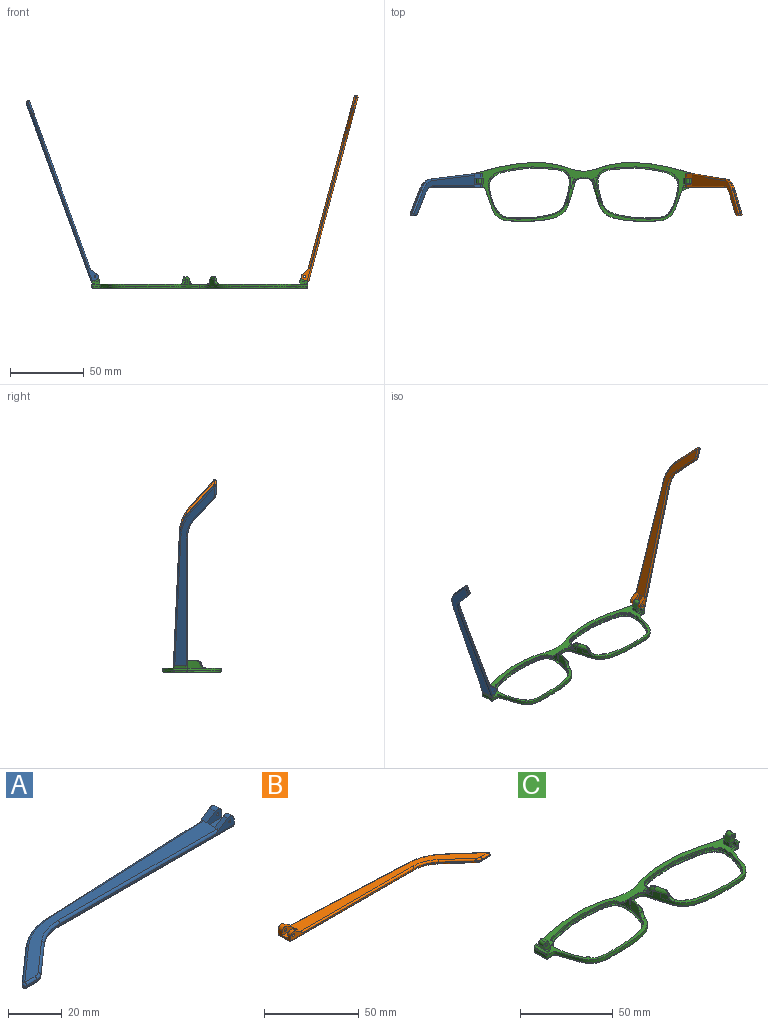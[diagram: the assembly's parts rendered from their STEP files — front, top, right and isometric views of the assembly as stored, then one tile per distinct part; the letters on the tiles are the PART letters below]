
ASSEMBLY  parts=3 mates=2
PART A: 43 faces, bbox 130.2x29.5x5.9 mm
  f0: plane 9.62x3.72mm, normal (1,0,0), area 24.7mm2, adj f1,f3,f4,f5,f10,f16,f18,f28
  f1: cylinder r=2.2mm len=3.45mm, axis (0,-1,0), area 11mm2, adj f0,f2,f4,f37
  f2: plane 6.01x3.91mm, normal (-0.55,0,0.84), area 12.7mm2, adj f1,f4,f9,f19,f37
  f3: plane 2.26x0.1mm, normal (0,0,1), area 0.1mm2, adj f0,f5,f18
  f4: plane 92.1x4.9mm, normal (0,-1,0), area 79.9mm2, adj f0,f1,f2,f14,f19,f36,f42
  f5: plane 93.42x4.13mm, normal (-0.04,1,0), area 64.8mm2, adj f0,f3,f11,f15,f17,f27,f28
  f6: plane 17.82x15.72mm, normal (-0.66,0.75,0), area 14.3mm2, adj f11,f12,f25,f30
  f7: plane 5.46x0.6mm, normal (0,-1,0), area 3.3mm2, adj f12,f13,f23,f32
  f8: plane 14.99x13.23mm, normal (0.66,-0.75,0), area 12mm2, adj f13,f14,f21,f34
  f9: plane 121.18x26.73mm, normal (0,0,1), area 627.7mm2, adj f2,f17,f19,f20,f21,f22,f23,f25
  f10: plane 129.1x27.08mm, normal (0,0,-1), area 686.5mm2, adj f0,f28,f29,f30,f32,f33,f34,f35
  f11: cylinder r=30mm len=18.52mm, axis (0,0,-1), area 12.2mm2, adj f5,f6,f26,f29
  f12: cylinder r=1mm len=1.75mm, axis (0,0,-1), area 1.5mm2, adj f6,f7,f24,f31
  f13: cylinder r=5mm len=3.31mm, axis (0,0,-1), area 2.2mm2, adj f7,f8,f22,f33
  f14: cylinder r=20mm len=13.23mm, axis (0,0,1), area 8.7mm2, adj f4,f8,f20,f35
  f15: plane 5.66x0.25mm, normal (0,0,-1), area 0.7mm2, adj f5,f17,f18
  f16: cylinder r=2.2mm len=3.45mm, axis (0,-1,0), area 14.8mm2, adj f0,f17,f18,f38
  f17: plane 6.01x3.91mm, normal (-0.55,0,0.84), area 16.9mm2, adj f5,f9,f15,f16,f18,f27,f38
  f18: plane 7.92x3.3mm, normal (0,1,0), area 15.9mm2, adj f0,f3,f15,f16,f17,f41
  f19: cylinder r=1mm len=84.18mm, axis (-1,0,0), area 131.4mm2, adj f2,f4,f9,f20
  f20: torus R=21mm, axis (0,0,1), area 23.1mm2, adj f9,f14,f19,f21
  f21: cylinder r=1mm len=15.65mm, axis (-0.75,-0.66,0), area 31.4mm2, adj f8,f9,f20,f22
  f22: torus R=4mm, axis (0,0,1), area 5.3mm2, adj f9,f13,f21,f23
  f23: cylinder r=1mm len=5.46mm, axis (-1,0,0), area 8.6mm2, adj f7,f9,f22,f24
  f24: sphere r=1mm, area 2.4mm2, adj f12,f23,f25
  f25: cylinder r=1mm len=18.48mm, axis (0.75,0.66,0), area 37.3mm2, adj f6,f9,f24,f26
  f26: torus R=29mm, axis (0,0,1), area 31.6mm2, adj f9,f11,f25,f27
  f27: cylinder r=1mm len=85.5mm, axis (1,0.04,0), area 133.5mm2, adj f5,f9,f17,f26
  f28: cylinder r=1mm len=93.46mm, axis (-1,-0.04,0), area 146.9mm2, adj f0,f5,f10,f29
  f29: torus R=29mm, axis (0,0,1), area 31.6mm2, adj f10,f11,f28,f30
  f30: cylinder r=1mm len=18.48mm, axis (-0.75,-0.66,0), area 37.3mm2, adj f6,f10,f29,f31
  f31: sphere r=1mm, area 2.4mm2, adj f12,f30,f32
  f32: cylinder r=1mm len=5.46mm, axis (1,0,0), area 8.6mm2, adj f7,f10,f31,f33
  f33: torus R=4mm, axis (0,0,1), area 5.3mm2, adj f10,f13,f32,f34
  f34: cylinder r=1mm len=15.65mm, axis (0.75,0.66,0), area 31.4mm2, adj f8,f10,f33,f35
  f35: torus R=21mm, axis (0,0,1), area 23.1mm2, adj f10,f14,f34,f36
  f36: cylinder r=1mm len=92.1mm, axis (1,0,0), area 144.7mm2, adj f0,f4,f10,f35
  f37: plane 7.92x4.7mm, normal (0,1,0), area 27mm2, adj f0,f1,f2,f39,f40,f42
  f38: plane 7.92x4.7mm, normal (0,-1,0), area 27mm2, adj f0,f16,f17,f39,f40,f41
  f39: plane 7.92x4.1mm, normal (0,0,1), area 32.5mm2, adj f0,f37,f38,f40
  f40: plane 4.1x1.4mm, normal (1,0,0), area 5.7mm2, adj f9,f37,f38,f39
  f41: cylinder r=0.5mm len=3.1mm, axis (0,-1,0), area 9.7mm2, adj f18,f38
  f42: cylinder r=0.5mm len=2.3mm, axis (0,-1,0), area 7.2mm2, adj f4,f37
PART B: 43 faces, bbox 130.2x29.5x5.9 mm
  f0: plane 9.62x3.72mm, normal (-1,0,0), area 24.7mm2, adj f1,f3,f4,f5,f10,f16,f18,f28
  f1: cylinder r=2.2mm len=3.45mm, axis (0,-1,0), area 11mm2, adj f0,f2,f4,f37
  f2: plane 6.01x3.91mm, normal (0.55,0,0.84), area 12.7mm2, adj f1,f4,f9,f19,f37
  f3: plane 2.26x0.1mm, normal (0,0,1), area 0.1mm2, adj f0,f5,f18
  f4: plane 92.1x4.9mm, normal (0,-1,0), area 78.2mm2, adj f0,f1,f2,f14,f19,f36,f42
  f5: plane 93.42x4.13mm, normal (0.04,1,0), area 64.8mm2, adj f0,f3,f11,f15,f17,f27,f28
  f6: plane 17.82x15.72mm, normal (0.66,0.75,0), area 14.3mm2, adj f11,f12,f25,f30
  f7: plane 5.46x0.6mm, normal (0,-1,0), area 3.3mm2, adj f12,f13,f23,f32
  f8: plane 14.99x13.23mm, normal (-0.66,-0.75,0), area 12mm2, adj f13,f14,f21,f34
  f9: plane 121.18x26.73mm, normal (0,0,1), area 627.7mm2, adj f2,f17,f19,f20,f21,f22,f23,f25
  f10: plane 129.1x27.08mm, normal (0,0,-1), area 686.5mm2, adj f0,f28,f29,f30,f32,f33,f34,f35
  f11: cylinder r=30mm len=18.52mm, axis (0,0,-1), area 12.2mm2, adj f5,f6,f26,f29
  f12: cylinder r=1mm len=1.75mm, axis (0,0,-1), area 1.5mm2, adj f6,f7,f24,f31
  f13: cylinder r=5mm len=3.31mm, axis (0,0,-1), area 2.2mm2, adj f7,f8,f22,f33
  f14: cylinder r=20mm len=13.23mm, axis (0,0,1), area 8.7mm2, adj f4,f8,f20,f35
  f15: plane 5.66x0.25mm, normal (0,0,-1), area 0.7mm2, adj f5,f17,f18
  f16: cylinder r=2.2mm len=3.45mm, axis (0,-1,0), area 14.8mm2, adj f0,f17,f18,f38
  f17: plane 6.01x3.91mm, normal (0.55,0,0.84), area 16.9mm2, adj f5,f9,f15,f16,f18,f27,f38
  f18: plane 7.92x3.3mm, normal (0,1,0), area 14.3mm2, adj f0,f3,f15,f16,f17,f41
  f19: cylinder r=1mm len=84.18mm, axis (1,0,0), area 131.4mm2, adj f2,f4,f9,f20
  f20: torus R=21mm, axis (0,0,1), area 23.1mm2, adj f9,f14,f19,f21
  f21: cylinder r=1mm len=15.65mm, axis (0.75,-0.66,0), area 31.4mm2, adj f8,f9,f20,f22
  f22: torus R=4mm, axis (0,0,1), area 5.3mm2, adj f9,f13,f21,f23
  f23: cylinder r=1mm len=5.46mm, axis (1,0,0), area 8.6mm2, adj f7,f9,f22,f24
  f24: sphere r=1mm, area 2.4mm2, adj f12,f23,f25
  f25: cylinder r=1mm len=18.48mm, axis (-0.75,0.66,0), area 37.3mm2, adj f6,f9,f24,f26
  f26: torus R=29mm, axis (0,0,1), area 31.6mm2, adj f9,f11,f25,f27
  f27: cylinder r=1mm len=85.5mm, axis (-1,0.04,0), area 133.5mm2, adj f5,f9,f17,f26
  f28: cylinder r=1mm len=93.46mm, axis (1,-0.04,0), area 146.9mm2, adj f0,f5,f10,f29
  f29: torus R=29mm, axis (0,0,1), area 31.6mm2, adj f10,f11,f28,f30
  f30: cylinder r=1mm len=18.48mm, axis (0.75,-0.66,0), area 37.3mm2, adj f6,f10,f29,f31
  f31: sphere r=1mm, area 2.4mm2, adj f12,f30,f32
  f32: cylinder r=1mm len=5.46mm, axis (-1,0,0), area 8.6mm2, adj f7,f10,f31,f33
  f33: torus R=4mm, axis (0,0,1), area 5.3mm2, adj f10,f13,f32,f34
  f34: cylinder r=1mm len=15.65mm, axis (-0.75,0.66,0), area 31.4mm2, adj f8,f10,f33,f35
  f35: torus R=21mm, axis (0,0,1), area 23.1mm2, adj f10,f14,f34,f36
  f36: cylinder r=1mm len=92.1mm, axis (-1,0,0), area 144.7mm2, adj f0,f4,f10,f35
  f37: plane 7.92x4.7mm, normal (0,1,0), area 25.4mm2, adj f0,f1,f2,f39,f40,f42
  f38: plane 7.92x4.7mm, normal (0,-1,0), area 25.4mm2, adj f0,f16,f17,f39,f40,f41
  f39: plane 7.92x4.1mm, normal (0,0,1), area 32.5mm2, adj f0,f37,f38,f40
  f40: plane 4.1x1.4mm, normal (-1,0,0), area 5.7mm2, adj f9,f37,f38,f39
  f41: cylinder r=0.88mm len=3.1mm, axis (0,-1,0), area 17mm2, adj f18,f38
  f42: cylinder r=0.88mm len=2.3mm, axis (0,-1,0), area 12.6mm2, adj f4,f37
PART C: 118 faces, bbox 148.1x40.9x17.9 mm
  f0: bspline ~1.82x1.22mm, area 0.7mm2, adj f2,f7,f37,f52
  f1: plane 147.69x40.46mm, normal (0,0,1), area 858.2mm2, adj f4,f5,f6,f7,f8,f12,f20,f23
  f2: bspline ~6.1x4.93mm, area 12.7mm2, adj f0,f7,f37,f41,f43,f52,f53
  f3: plane 4.46x1.45mm, normal (0,0,1), area 0.1mm2, adj f7,f38
  f4: plane 1.23x0.04mm, normal (0,0,1), area 0mm2, adj f1,f7,f22
  f5: plane 6.97x5.07mm, normal (0,1,0), area 22.7mm2, adj f1,f20,f21,f25,f27,f28,f30,f31
  f6: plane 3.2x2.36mm, normal (0,-1,0), area 5.7mm2, adj f1,f20,f26,f29
  f7: extruded ~73.26x39.84mm, area 292.7mm2, adj f0,f1,f2,f3,f4,f8,f13,f14
  f8: extruded ~35.39x5.69mm, area 72.2mm2, adj f1,f7,f18,f67
  f9: plane 144.78x37.85mm, normal (0,0,-1), area 582.4mm2, adj f13,f15,f17,f18,f19,f71,f73,f75
  f10: plane 56.06x35.45mm, normal (0,0,1), area 127mm2, adj f11,f19
  f11: extruded ~55.69x35.36mm, area 160.5mm2, adj f10,f12
  f12: extruded ~55.69x35.36mm, area 226.3mm2, adj f1,f11,f39,f40,f41,f42,f43,f44
  f13: bspline ~73.27x30.39mm, area 161.7mm2, adj f7,f9,f14,f71
  f14: bspline ~1x1mm, area 0.8mm2, adj f7,f13,f15
  f15: bspline ~8.99x1.23mm, area 12.6mm2, adj f7,f9,f14,f16
  f16: bspline ~1.04x1mm, area 0.7mm2, adj f7,f15,f17
  f17: bspline ~45.86x8.59mm, area 59.8mm2, adj f7,f9,f16,f18
  f18: bspline ~37.01x6.7mm, area 56.6mm2, adj f8,f9,f17,f76
  f19: bspline ~56.23x35.9mm, area 235.3mm2, adj f9,f10
  f20: plane 4x2.36mm, normal (-1,0,0), area 9.5mm2, adj f1,f5,f6,f21
  f21: plane 4x0.02mm, normal (0.34,0,0.94), area 0.1mm2, adj f5,f20,f28
  f22: plane 2.76x2.53mm, normal (0,-1,0), area 3.9mm2, adj f4,f26,f27,f35,f56
  f23: plane 7.67x1.6mm, normal (0.94,0,-0.34), area 13mm2, adj f1,f35,f36,f56
  f24: plane 2.1x1.69mm, normal (0,1,0), area 2.8mm2, adj f1,f25,f27,f36,f56
  f25: plane 3.3x2.1mm, normal (-1,0,0), area 6.9mm2, adj f1,f5,f24,f27
  f26: plane 2.35x2.1mm, normal (-1,0,0), area 4.9mm2, adj f1,f6,f22,f27,f29
  f27: plane 9.65x1.24mm, normal (0,0,1), area 8.2mm2, adj f5,f22,f24,f25,f26,f29,f30,f56
  f28: plane 4x3.31mm, normal (-0.94,0,0.34), area 14.1mm2, adj f5,f21,f29,f32
  f29: plane 5.77x5.06mm, normal (0,-1,0), area 17mm2, adj f6,f26,f27,f28,f30,f31,f32,f33
  f30: plane 4x2.21mm, normal (0.94,0,-0.34), area 9.4mm2, adj f5,f27,f29,f33
  f31: plane 4x0.01mm, normal (0.34,0,0.94), area 0mm2, adj f5,f29,f32,f33
  f32: cylinder r=1.98mm len=4mm, axis (0,1,0), area 12.4mm2, adj f5,f28,f29,f31
  f33: cylinder r=1.98mm len=4mm, axis (0,-1,0), area 12.4mm2, adj f5,f29,f30,f31
  f34: cylinder r=0.88mm len=4mm, axis (0,-1,0), area 22mm2, adj f5,f29
  f35: cone r=1mm half-angle=20deg, axis (0,0,1), area 2.3mm2, adj f1,f22,f23,f56
  f36: cylinder r=1mm len=2.28mm, axis (-0.34,0,-0.94), area 3mm2, adj f1,f23,f24,f56
  f37: extruded ~3.67x3.11mm, area 5.9mm2, adj f0,f2,f7,f59
  f38: extruded ~4.44x3.32mm, area 15.1mm2, adj f3,f7,f42,f43,f55
  f39: extruded ~4.98x1.37mm, area 6.6mm2, adj f12,f41
  f40: plane 3.63x0.97mm, normal (0,0,1), area 0.3mm2, adj f12,f41,f43
  f41: bspline ~15.5x15.35mm, area 6.4mm2, adj f2,f12,f39,f40,f54
  f42: bspline ~7.26x7.26mm, area 6.3mm2, adj f12,f38,f43,f55
  f43: bspline ~10.29x4.84mm, area 21.4mm2, adj f2,f7,f12,f38,f40,f42
  f44: plane 3.19x1.37mm, normal (0,0,-1), area 2.1mm2, adj f12,f45
  f45: cylinder r=2.28mm len=3.17mm, axis (0,0,1), area 2.1mm2, adj f1,f12,f44,f54
  f46: plane 3.14x2.79mm, normal (0,0,-1), area 3.9mm2, adj f12,f47
  f47: cylinder r=2.28mm len=3.13mm, axis (0,0,1), area 2.5mm2, adj f1,f12,f46
  f48: plane 1.79x1.31mm, normal (0,0,-1), area 0.9mm2, adj f12,f49
  f49: cylinder r=1.3mm len=1.78mm, axis (0,0,1), area 1.3mm2, adj f1,f12,f48
  f50: plane 1.95x1.68mm, normal (0,0,-1), area 1.5mm2, adj f12,f51
  f51: cylinder r=1.3mm len=1.93mm, axis (0,0,1), area 1.5mm2, adj f1,f12,f50
  f52: bspline ~2.66x2.04mm, area 1.9mm2, adj f0,f2,f7,f53,f58
  f53: bspline ~3.55x3.47mm, area 3.7mm2, adj f1,f2,f52,f54,f58
  f54: bspline ~5.1x3.97mm, area 7.9mm2, adj f1,f12,f41,f45,f53
  f55: bspline ~3.7x3.66mm, area 7.8mm2, adj f1,f7,f12,f38,f42
  f56: plane 9.71x1.44mm, normal (0.34,0,0.94), area 13.9mm2, adj f22,f23,f24,f27,f35,f36
  f57: bspline ~6.38x2.14mm, area 2.6mm2, adj f1,f7,f58,f115
  f58: bspline ~2.1x1.46mm, area 0.6mm2, adj f7,f52,f53,f57
  f59: bspline ~5.24x1.75mm, area 0mm2, adj f7,f37
  f60: bspline ~2.19x1.4mm, area 0.7mm2, adj f61,f66,f95,f110
  f61: bspline ~6.1x4.93mm, area 12.6mm2, adj f60,f66,f95,f99,f101,f110,f111
  f62: plane 4.46x1.45mm, normal (0,0,1), area 0.1mm2, adj f66,f96
  f63: plane 1.23x0.04mm, normal (0,0,1), area 0mm2, adj f1,f66,f80
  f64: plane 6.97x5.07mm, normal (0,1,0), area 22.7mm2, adj f1,f78,f79,f83,f85,f86,f88,f89
  f65: plane 3.2x2.36mm, normal (0,-1,0), area 5.7mm2, adj f1,f78,f84,f87
  f66: extruded ~73.26x39.84mm, area 292.7mm2, adj f1,f7,f60,f61,f62,f63,f67,f71
  f67: extruded ~35.39x5.69mm, area 72.2mm2, adj f1,f8,f66,f76
  f68: plane 56.06x35.45mm, normal (0,0,1), area 127mm2, adj f69,f77
  f69: extruded ~55.69x35.36mm, area 160.5mm2, adj f68,f70
  f70: extruded ~55.69x35.36mm, area 226.4mm2, adj f1,f69,f97,f98,f99,f100,f101,f102
  f71: bspline ~73.83x30.39mm, area 161.7mm2, adj f9,f13,f66,f72
  f72: bspline ~1x1mm, area 0.8mm2, adj f66,f71,f73
  f73: bspline ~8.99x1.23mm, area 12.6mm2, adj f9,f66,f72,f74
  f74: bspline ~1.04x1mm, area 0.8mm2, adj f66,f73,f75
  f75: bspline ~45.86x8.59mm, area 59.8mm2, adj f9,f66,f74,f76
  f76: bspline ~37.01x6.7mm, area 56.6mm2, adj f9,f18,f67,f75
  f77: bspline ~56.22x35.9mm, area 235.3mm2, adj f9,f68
  f78: plane 4x2.36mm, normal (1,0,0), area 9.5mm2, adj f1,f64,f65,f79
  f79: plane 4x0.02mm, normal (-0.34,0,0.94), area 0.1mm2, adj f64,f78,f86
  f80: plane 2.76x2.53mm, normal (0,-1,0), area 3.9mm2, adj f63,f84,f85,f93,f114
  f81: plane 7.67x1.6mm, normal (-0.94,0,-0.34), area 13mm2, adj f1,f93,f94,f114
  f82: plane 2.1x1.69mm, normal (0,1,0), area 2.8mm2, adj f1,f83,f85,f94,f114
  f83: plane 3.3x2.1mm, normal (1,0,0), area 6.9mm2, adj f1,f64,f82,f85
  f84: plane 2.35x2.1mm, normal (1,0,0), area 4.9mm2, adj f1,f65,f80,f85,f87
  f85: plane 9.65x1.24mm, normal (0,0,1), area 8.2mm2, adj f64,f80,f82,f83,f84,f87,f88,f114
  f86: plane 4x3.31mm, normal (0.94,0,0.34), area 14.1mm2, adj f64,f79,f87,f90
  f87: plane 5.77x5.06mm, normal (0,-1,0), area 17mm2, adj f65,f84,f85,f86,f88,f89,f90,f91
  f88: plane 4x2.21mm, normal (-0.94,0,-0.34), area 9.4mm2, adj f64,f85,f87,f91
  f89: plane 4x0.01mm, normal (-0.34,0,0.94), area 0mm2, adj f64,f87,f90,f91
  f90: cylinder r=1.98mm len=4mm, axis (0,1,0), area 12.4mm2, adj f64,f86,f87,f89
  f91: cylinder r=1.98mm len=4mm, axis (0,-1,0), area 12.4mm2, adj f64,f87,f88,f89
  f92: cylinder r=0.88mm len=4mm, axis (0,-1,0), area 22mm2, adj f64,f87
  f93: cone r=1mm half-angle=20deg, axis (0,0,1), area 2.3mm2, adj f1,f80,f81,f114
  f94: cylinder r=1mm len=2.28mm, axis (0.34,0,-0.94), area 3mm2, adj f1,f81,f82,f114
  f95: extruded ~3.67x3.11mm, area 5.9mm2, adj f60,f61,f66,f117
  f96: extruded ~4.44x3.32mm, area 15.1mm2, adj f62,f66,f100,f101,f113
  f97: extruded ~4.98x1.36mm, area 6.6mm2, adj f70,f99
  f98: plane 3.63x0.97mm, normal (0,0,1), area 0.3mm2, adj f70,f99,f101
  f99: bspline ~15.5x15.35mm, area 6.4mm2, adj f61,f70,f97,f98,f112
  f100: bspline ~7.26x7.26mm, area 6.2mm2, adj f70,f96,f101,f113
  f101: bspline ~10.29x4.84mm, area 21.5mm2, adj f61,f66,f70,f96,f98,f100
  f102: plane 3.19x1.37mm, normal (0,0,-1), area 2.1mm2, adj f70,f103
  f103: cylinder r=2.28mm len=3.17mm, axis (0,0,1), area 2.1mm2, adj f1,f70,f102,f112
  f104: plane 3.14x2.79mm, normal (0,0,-1), area 3.9mm2, adj f70,f105
  f105: cylinder r=2.28mm len=3.13mm, axis (0,0,1), area 2.5mm2, adj f1,f70,f104
  f106: plane 1.79x1.31mm, normal (0,0,-1), area 0.9mm2, adj f70,f107
  f107: cylinder r=1.3mm len=1.78mm, axis (0,0,1), area 1.3mm2, adj f1,f70,f106
  f108: plane 1.95x1.68mm, normal (0,0,-1), area 1.5mm2, adj f70,f109
  f109: cylinder r=1.3mm len=1.93mm, axis (0,0,1), area 1.5mm2, adj f1,f70,f108
  f110: bspline ~2.65x2.03mm, area 1.9mm2, adj f60,f61,f66,f111,f116
  f111: bspline ~3.55x3.47mm, area 3.7mm2, adj f1,f61,f110,f112,f116
  f112: bspline ~5.94x4.42mm, area 7.9mm2, adj f1,f70,f99,f103,f111
  f113: bspline ~3.7x3.66mm, area 7.8mm2, adj f1,f66,f70,f96,f100
  f114: plane 9.71x1.44mm, normal (-0.34,0,0.94), area 13.9mm2, adj f80,f81,f82,f85,f93,f94
  f115: bspline ~6.38x2.14mm, area 2.6mm2, adj f1,f57,f66,f116
  f116: bspline ~2.1x1.46mm, area 0.6mm2, adj f66,f110,f111,f115
  f117: bspline ~5.24x1.75mm, area 0mm2, adj f66,f95
PLACE A rot(axis=(0,1,0),70deg) t=(-84.77,-5.75,56)mm
PLACE B rot(axis=(0,-1,0),75deg) t=(68.2,-5.75,-61.61)mm
PLACE C t=(10.15,-1.13,-5.77)mm
MATE revolute A.f1 <-> C.f90  axis (0,-1,0) through (-60.89,2.72,1.22)mm
MATE revolute B.f41 <-> C.f33  axis (0,-1,0) through (81.2,2.72,1.21)mm
